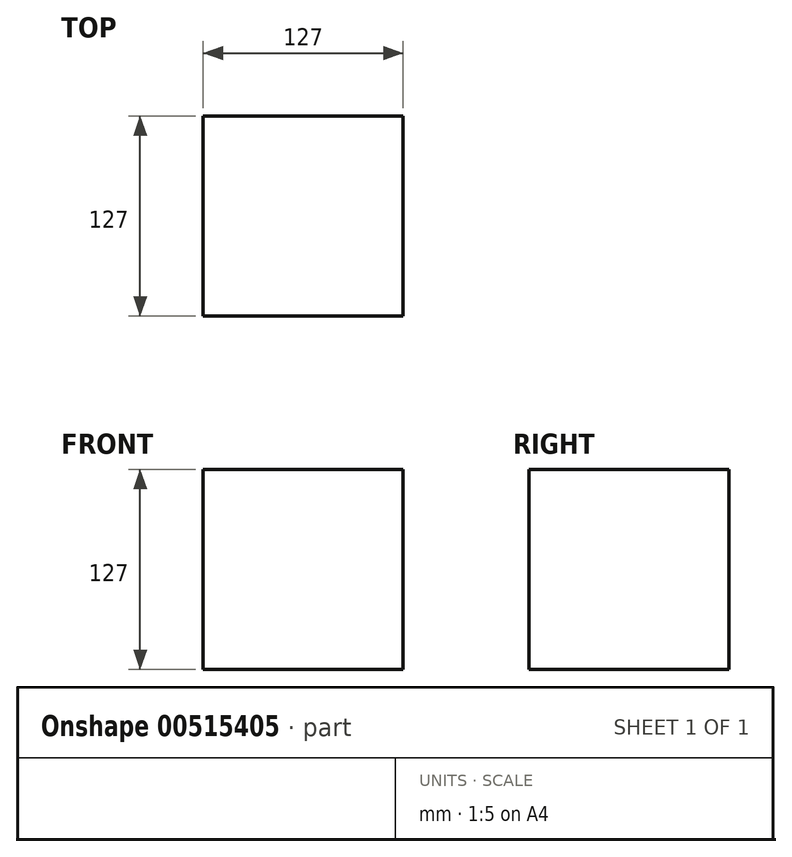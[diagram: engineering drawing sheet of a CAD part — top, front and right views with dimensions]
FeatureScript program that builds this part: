
annotation { "Feature Type Name" : "Feature", "Feature Type Description" : "" }
export const myFeature = defineFeature(function(context is Context, id is Id, definition is map)
    precondition{}
    {
        {
            var Q0;
            Q0=qCreatedBy(makeId("Top.planeOp"),FACE);
            var sketch = newSketch(context, id + "F0", { "sketchPlane" : qUnion([Q0])});
            skLineSegment(sketch, "E0.bottom", {"start": v(63.5, 63.5) * mm, "end": v(-63.5, 63.5) * mm});
            skLineSegment(sketch, "E0.top", {"start": v(63.5, -63.5) * mm, "end": v(-63.5, -63.5) * mm});
            skLineSegment(sketch, "E0.left", {"start": v(63.5, 63.5) * mm, "end": v(63.5, -63.5) * mm});
            skLineSegment(sketch, "E0.right", {"start": v(-63.5, 63.5) * mm, "end": v(-63.5, -63.5) * mm});
            skPoint(sketch, "E0.middle", {"position": v(0, 0) * mm});
            skSolve(sketch);
        }
        {
            var Q0;
            Q0=makeQuery(id+"F0.imprint","IMPRINT",FACE,{"disambiguationData":[TD([[makeQuery(id+"F0.imprint","IMPRINT",EDGE,{"derivedFrom":sQuery(id+"F0.wireOp",EDGE,"E0.bottom")}),1.0]])]});
            extrude(context, id + "F1", {"entities" : qUnion([Q0]), "depth" : 127 * mm, "offsetDistance" : 25.4 * mm});
        }
    });
